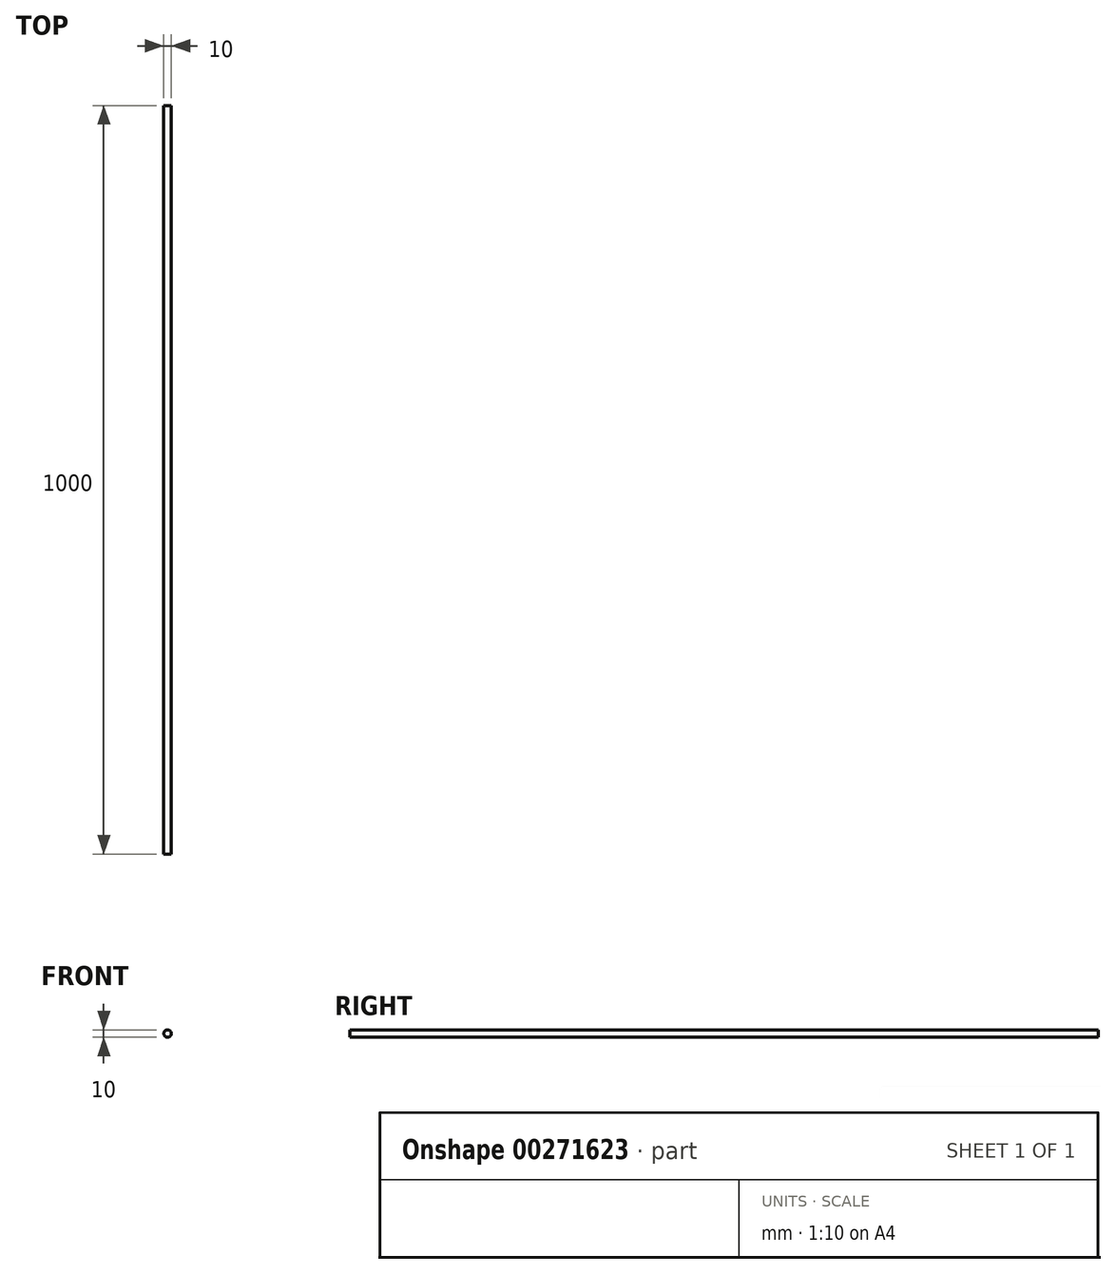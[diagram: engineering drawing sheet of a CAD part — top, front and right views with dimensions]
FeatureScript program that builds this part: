
annotation { "Feature Type Name" : "Feature", "Feature Type Description" : "" }
export const myFeature = defineFeature(function(context is Context, id is Id, definition is map)
    precondition{}
    {
        {
            var Q0;
            Q0=qCreatedBy(makeId("Front.planeOp"),FACE);
            var sketch = newSketch(context, id + "F0", { "sketchPlane" : qUnion([Q0])});
            skCircle(sketch, "E0", {"center": v(0, 0) * mm, "radius": 5 * mm});
            skSolve(sketch);
        }
        {
            var Q0;
            Q0=makeQuery(id+"F0.imprint","IMPRINT",FACE,{"disambiguationData":[TD([[makeQuery(id+"F0.imprint","IMPRINT",EDGE,{"derivedFrom":sQuery(id+"F0.wireOp",EDGE,"E0")}),1.0]])]});
            var Q1;
            Q1=sQuery(id+"F0.wireOp",EDGE,"E0");
            extrude(context, id + "F1", {"entities" : qUnion([Q0]), "surfaceEntities" : qUnion([Q1]), "depth" : 1000 * mm});
        }
    });
